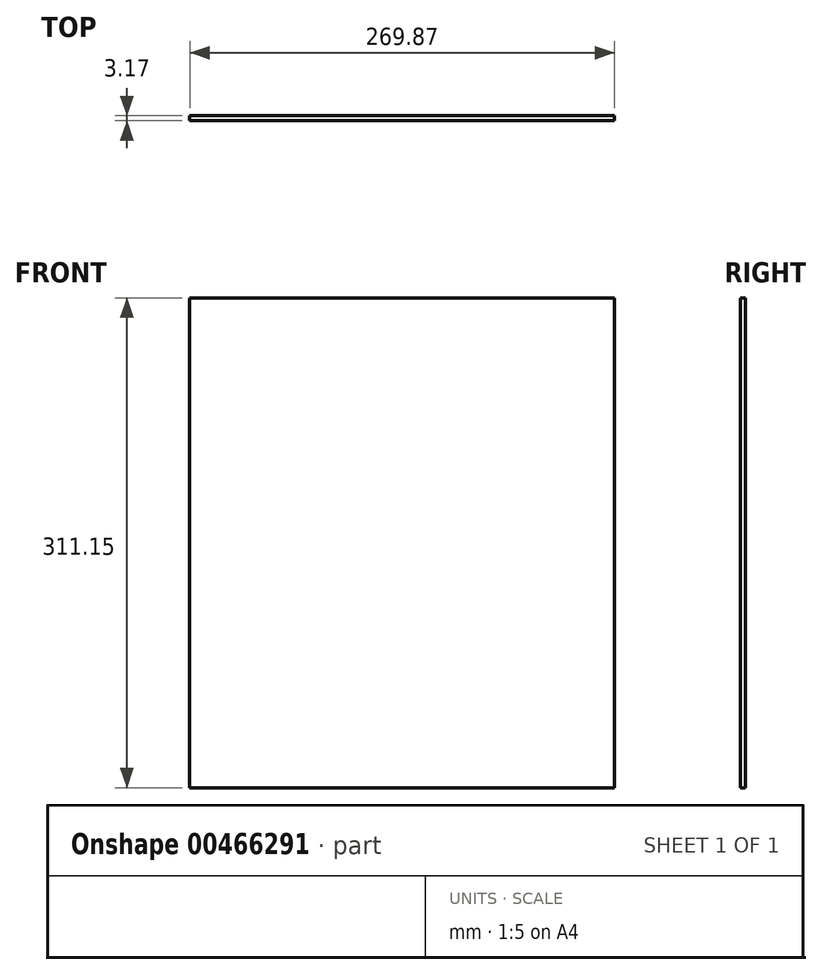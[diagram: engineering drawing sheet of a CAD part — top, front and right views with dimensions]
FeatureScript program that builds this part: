
annotation { "Feature Type Name" : "Feature", "Feature Type Description" : "" }
export const myFeature = defineFeature(function(context is Context, id is Id, definition is map)
    precondition{}
    {
        {
            var Q0;
            Q0=qCreatedBy(makeId("Front.planeOp"),FACE);
            var sketch = newSketch(context, id + "F0", { "sketchPlane" : qUnion([Q0])});
            skLineSegment(sketch, "E0", {"start": v(-367.72, 397.8) * mm, "end": v(-97.85, 397.8) * mm});
            skLineSegment(sketch, "E1", {"start": v(-97.85, 397.8) * mm, "end": v(-97.85, 86.66) * mm});
            skLineSegment(sketch, "E2", {"start": v(-97.85, 86.66) * mm, "end": v(-367.72, 86.66) * mm});
            skLineSegment(sketch, "E3", {"start": v(-367.72, 86.66) * mm, "end": v(-367.72, 397.8) * mm});
            skSolve(sketch);
        }
        {
            var Q0;
            Q0=qSketchRegion(id+"F0",true);
            extrude(context, id + "F1", {"entities" : qUnion([Q0]), "depth" : 3.17 * mm, "offsetDistance" : 25.4 * mm});
        }
    });
